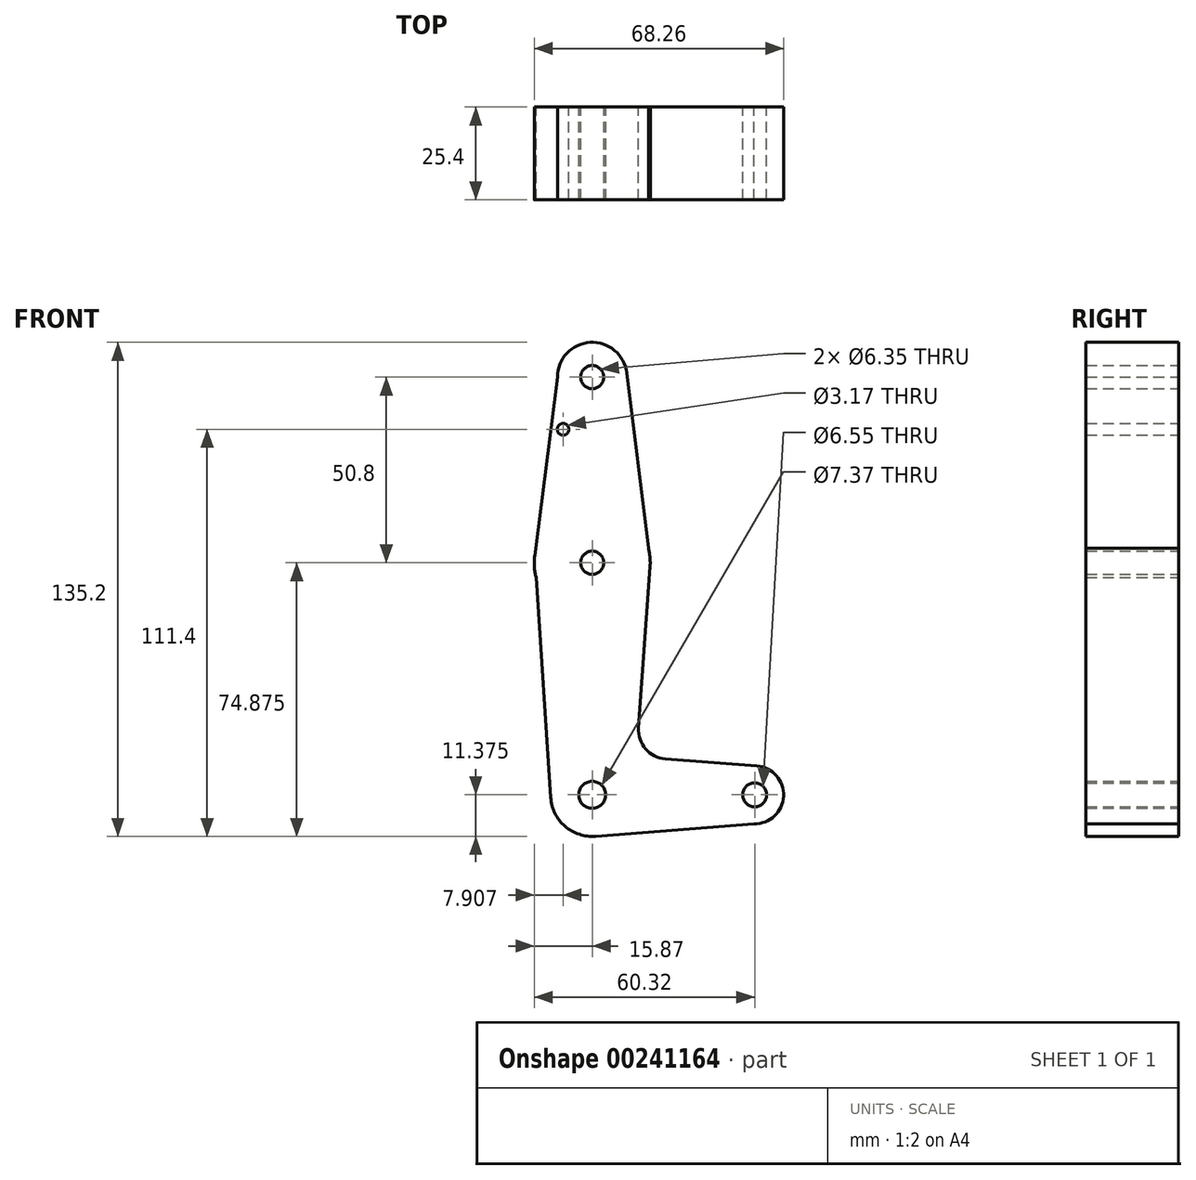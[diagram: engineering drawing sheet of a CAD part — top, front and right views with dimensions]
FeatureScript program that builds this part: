
annotation { "Feature Type Name" : "Feature", "Feature Type Description" : "" }
export const myFeature = defineFeature(function(context is Context, id is Id, definition is map)
    precondition{}
    {
        {
            var Q0;
            Q0=qCreatedBy(makeId("Front.planeOp"),FACE);
            var sketch = newSketch(context, id + "F0", { "sketchPlane" : qUnion([Q0])});
            skCircle(sketch, "E0", {"center": v(0, 73.93) * mm, "radius": 9.53 * mm});
            skCircle(sketch, "E1", {"center": v(0, 73.93) * mm, "radius": 3.18 * mm});
            skCircle(sketch, "E2", {"center": v(0, 23.13) * mm, "radius": 15.88 * mm});
            skCircle(sketch, "E3", {"center": v(0, -40.37) * mm, "radius": 11.38 * mm});
            skCircle(sketch, "E4", {"center": v(0, -40.37) * mm, "radius": 3.68 * mm});
            skCircle(sketch, "E5", {"center": v(-7.96, 59.66) * mm, "radius": 1.59 * mm});
            skCircle(sketch, "E6", {"center": v(0, 23.13) * mm, "radius": 3.18 * mm});
            skLineSegment(sketch, "E7", {"start": v(0, -40.37) * mm, "end": v(44.45, -40.37) * mm});
            skCircle(sketch, "E8", {"center": v(44.45, -40.37) * mm, "radius": 7.94 * mm});
            skCircle(sketch, "E9", {"center": v(44.45, -40.37) * mm, "radius": 3.28 * mm});
            skLineSegment(sketch, "E10", {"start": v(0, 73.93) * mm, "end": v(0, 23.13) * mm});
            skLineSegment(sketch, "E11", {"start": v(0, 23.13) * mm, "end": v(0, -40.37) * mm});
            skLineSegment(sketch, "E12", {"start": v(-9.52, 73.93) * mm, "end": v(-15.75, 25.14) * mm});
            skLineSegment(sketch, "E13", {"start": v(-15.75, 25.14) * mm, "end": v(-15.34, 19.06) * mm});
            skLineSegment(sketch, "E14", {"start": v(20, -30.53) * mm, "end": v(45.06, -32.45) * mm});
            skLineSegment(sketch, "E15", {"start": v(44.29, -48.3) * mm, "end": v(0, -51.78) * mm});
            skLineSegment(sketch, "E16", {"start": v(12.69, -22.03) * mm, "end": v(15.83, 22) * mm});
            skLineSegment(sketch, "E17", {"start": v(15.37, 27.12) * mm, "end": v(9.45, 75.1) * mm});
            skArc(sketch, "E18.filletArc", {"start": v(12.69, -22.03) * mm, "mid": v(14.6, -27.79) * mm, "end": v(20, -30.53) * mm});
            skLineSegment(sketch, "E19", {"start": v(-15.34, 19.06) * mm, "end": v(-11.35, -41.12) * mm});
            skSolve(sketch);
        }
        {
            var Q0;
            Q0 = qSketchRegion(id + "F0", true);
            var Q1;
            {var subQ0=sQuery(id+"F0.wireOp",EDGE,"E11");var subQ1=sQuery(id+"F0.wireOp",EDGE,"E3");var subQ2=makeQuery(id+"F0.imprint","INTERSECT",VERTEX,{"derivedFrom":[subQ1,subQ0]});Q1=makeQuery(id+"F0.imprint","IMPRINT",FACE,{"disambiguationData":[TD([[makeQuery(id+"F0.imprint","IMPRINT",EDGE,{"disambiguationData":[TD([[subQ2,1.0]])],"derivedFrom":subQ1}),1.0]])]});}
            extrude(context, id + "F1", {"entities" : qUnion([Q0, Q1]), "depth" : 25.4 * mm});
        }
    });
